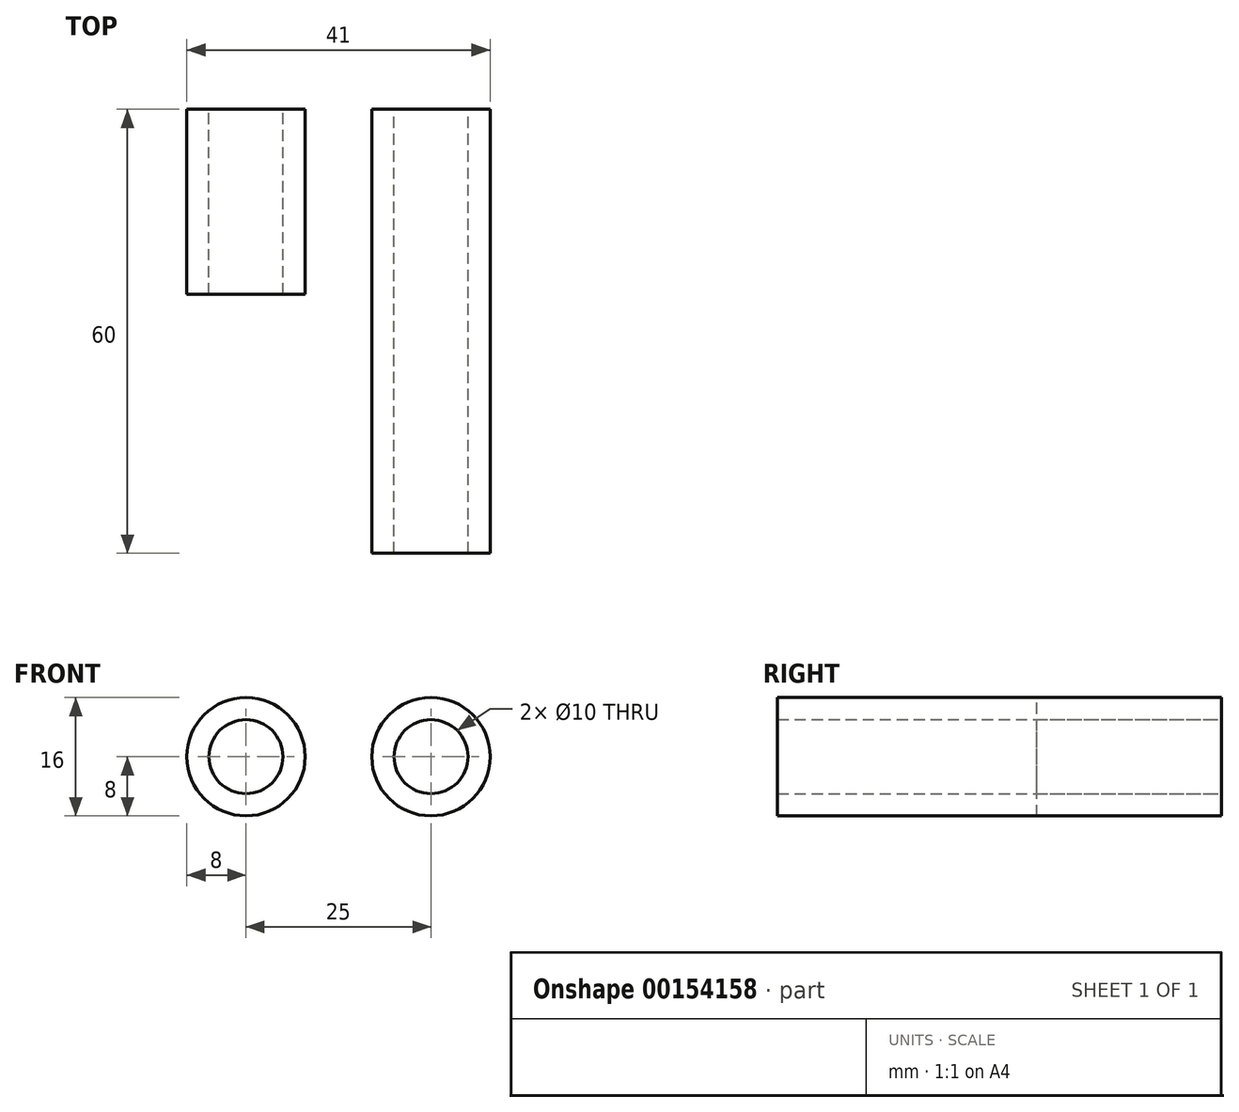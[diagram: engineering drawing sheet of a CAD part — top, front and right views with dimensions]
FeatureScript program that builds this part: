
annotation { "Feature Type Name" : "Feature", "Feature Type Description" : "" }
export const myFeature = defineFeature(function(context is Context, id is Id, definition is map)
    precondition{}
    {
        {
            var Q0;
            Q0=qCreatedBy(makeId("Front.planeOp"),FACE);
            var sketch = newSketch(context, id + "F0", { "sketchPlane" : qUnion([Q0])});
            skCircle(sketch, "E0", {"center": v(0, 0) * mm, "radius": 8 * mm});
            skCircle(sketch, "E1", {"center": v(0, 0) * mm, "radius": 5 * mm});
            skSolve(sketch);
        }
        {
            var Q0;
            Q0 = qSketchRegion(id + "F0", true);
            extrude(context, id + "F1", {"entities" : qUnion([Q0]), "depth" : 25 * mm});
        }
        {
            var Q0;
            Q0=qCreatedBy(makeId("Front.planeOp"),FACE);
            var sketch = newSketch(context, id + "F2", { "sketchPlane" : qUnion([Q0])});
            skPoint(sketch, "E2", {"position": v(25, 0) * mm});
            skCircle(sketch, "E3", {"center": v(25, 0) * mm, "radius": 8 * mm});
            skCircle(sketch, "E4", {"center": v(25, 0) * mm, "radius": 5 * mm});
            skSolve(sketch);
        }
        {
            var Q0;
            Q0 = qSketchRegion(id + "F2", true);
            extrude(context, id + "F3", {"entities" : qUnion([Q0]), "depth" : 60 * mm});
        }
    });
